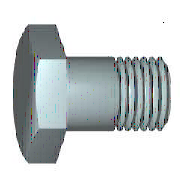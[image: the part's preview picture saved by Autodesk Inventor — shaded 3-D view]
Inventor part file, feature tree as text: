
AUTODESK INVENTOR PART (.ipt)
format: ipt  version: 2020 (Build 240168000, 168)  size: 192,000 bytes
history: native  units: mm (DEFAULTED — no unit token found)
features: sketch x3, extrude x1, chamfer x1, plane x1
ambient origin geometry x7: Origin, YZ Plane, XZ Plane, X Axis, Y Axis, Z Axis, Center Point
bodies: Solid1 (feature_tree), Body (feature_tree)
feature tree (6):
  extrude  "Head"  Depth=14.0mm
  chamfer  "Chamfer1"  Distance=2.4mm
  plane  "Work Plane1"
  sketch  "Sketch1"  dims[d0=40.0mm d1=14.0mm]
  sketch  "Sketch2"  dims[d2=4.0mm]
  sketch  "Sketch4"  dims[d12=90.0deg d3=2.4mm d4=0.0mm d5=30.0deg d21=90.0deg d6=0.429415mm d7=0.429515mm d8=0.0mm d9=0.4001mm d10=5.88mm d11=7.0mm d13=0.429515mm d14=4.0mm d15=14.0mm d16=0.0mm d19=7.0mm d55=45.0deg d57=0.0mm d58=0.0mm]
